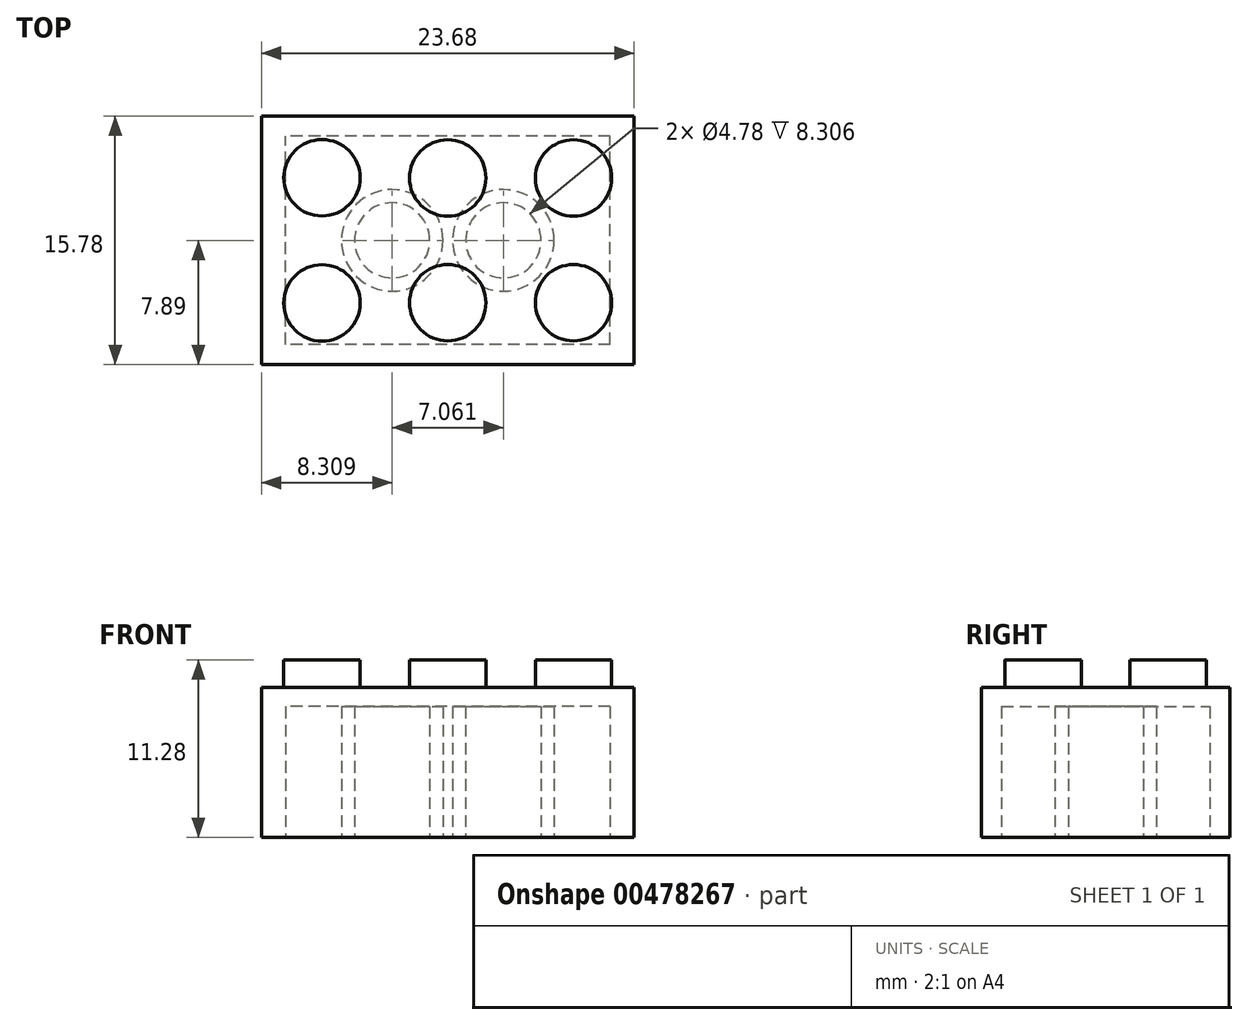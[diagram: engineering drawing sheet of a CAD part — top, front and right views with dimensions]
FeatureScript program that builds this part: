
annotation { "Feature Type Name" : "Feature", "Feature Type Description" : "" }
export const myFeature = defineFeature(function(context is Context, id is Id, definition is map)
    precondition{}
    {
        {
            var Q0;
            Q0=qCreatedBy(makeId("Top.planeOp"),FACE);
            var sketch = newSketch(context, id + "F0", { "sketchPlane" : qUnion([Q0])});
            skLineSegment(sketch, "E0.bottom", {"start": v(11.84, 7.89) * mm, "end": v(-11.84, 7.89) * mm});
            skLineSegment(sketch, "E0.top", {"start": v(11.84, -7.89) * mm, "end": v(-11.84, -7.89) * mm});
            skLineSegment(sketch, "E0.left", {"start": v(11.84, 7.89) * mm, "end": v(11.84, -7.89) * mm});
            skLineSegment(sketch, "E0.right", {"start": v(-11.84, 7.89) * mm, "end": v(-11.84, -7.89) * mm});
            skPoint(sketch, "E0.middle", {"position": v(0, 0) * mm});
            skSolve(sketch);
        }
        {
            var Q0;
            Q0=makeQuery(id+"F0.imprint","IMPRINT",FACE,{"disambiguationData":[TD([[makeQuery(id+"F0.imprint","IMPRINT",EDGE,{"derivedFrom":sQuery(id+"F0.wireOp",EDGE,"E0.bottom")}),1.0]])]});
            extrude(context, id + "F1", {"entities" : qUnion([Q0]), "endBound" : BoundingType.SYMMETRIC, "depth" : 9.52 * mm, "offsetDistance" : 25.4 * mm});
        }
        {
            var Q0;
            Q0=makeQuery(id+"F1.opExtrude","CAP_FACE",FACE,{"disambiguationData":[OSD([sQuery(id+"F0.wireOp",EDGE,"E0.bottom"),sQuery(id+"F0.wireOp",EDGE,"E0.top"),sQuery(id+"F0.wireOp",EDGE,"E0.left"),sQuery(id+"F0.wireOp",EDGE,"E0.right")])],"isStart":false});
            var sketch = newSketch(context, id + "F2", { "sketchPlane" : qUnion([Q0])});
            skCircle(sketch, "E1", {"center": v(-7.99, 3.98) * mm, "radius": 2.43 * mm});
            skCircle(sketch, "E2", {"center": v(0, 3.96) * mm, "radius": 2.43 * mm});
            skCircle(sketch, "E3", {"center": v(7.99, 3.96) * mm, "radius": 2.43 * mm});
            skCircle(sketch, "E4", {"center": v(7.99, -3.96) * mm, "radius": 2.43 * mm});
            skCircle(sketch, "E5", {"center": v(0, -3.96) * mm, "radius": 2.43 * mm});
            skCircle(sketch, "E6", {"center": v(-7.99, -3.98) * mm, "radius": 2.43 * mm});
            skSolve(sketch);
        }
        {
            var Q0;
            Q0 = qSketchRegion(id + "F2", true);
            extrude(context, id + "F3", {"entities" : qUnion([Q0]), "operationType" : NewBodyOperationType.ADD, "depth" : 1.75 * mm, "offsetDistance" : 25.4 * mm});
        }
        {
            var Q0;
            Q0=makeQuery(id+"F1.opExtrude","CAP_FACE",FACE,{"disambiguationData":[OSD([sQuery(id+"F0.wireOp",EDGE,"E0.bottom"),sQuery(id+"F0.wireOp",EDGE,"E0.top"),sQuery(id+"F0.wireOp",EDGE,"E0.left"),sQuery(id+"F0.wireOp",EDGE,"E0.right")])],"isStart":true});
            var sketch = newSketch(context, id + "F4", { "sketchPlane" : qUnion([Q0])});
            skLineSegment(sketch, "E7.bottom", {"start": v(10.31, 6.62) * mm, "end": v(-10.31, 6.62) * mm});
            skLineSegment(sketch, "E7.top", {"start": v(10.31, -6.62) * mm, "end": v(-10.31, -6.62) * mm});
            skLineSegment(sketch, "E7.left", {"start": v(10.31, 6.62) * mm, "end": v(10.31, -6.62) * mm});
            skLineSegment(sketch, "E7.right", {"start": v(-10.31, 6.62) * mm, "end": v(-10.31, -6.62) * mm});
            skPoint(sketch, "E7.middle", {"position": v(0, 0) * mm});
            skSolve(sketch);
        }
        {
            var Q0;
            Q0=makeQuery(id+"F4.imprint","IMPRINT",FACE,{"disambiguationData":[TD([[makeQuery(id+"F4.imprint","IMPRINT",EDGE,{"derivedFrom":sQuery(id+"F4.wireOp",EDGE,"E7.bottom")}),1.0]])]});
            var sketch = newSketch(context, id + "F5", { "sketchPlane" : qUnion([Q0])});
            skCircle(sketch, "E8", {"center": v(-3.53, 0) * mm, "radius": 3.23 * mm});
            skCircle(sketch, "E9", {"center": v(3.53, 0) * mm, "radius": 3.23 * mm});
            skSolve(sketch);
        }
        {
            var Q0;
            Q0=makeQuery(id+"F4.imprint","IMPRINT",FACE,{"disambiguationData":[TD([[makeQuery(id+"F4.imprint","IMPRINT",EDGE,{"derivedFrom":sQuery(id+"F4.wireOp",EDGE,"E7.bottom")}),1.0]])]});
            var sketch = newSketch(context, id + "F6", { "sketchPlane" : qUnion([Q0])});
            skCircle(sketch, "E10", {"center": v(-3.53, 0) * mm, "radius": 2.39 * mm});
            skCircle(sketch, "E11", {"center": v(3.53, 0) * mm, "radius": 2.39 * mm});
            skSolve(sketch);
        }
        {
            var Q0;
            Q0=makeQuery(id+"F4.imprint","IMPRINT",FACE,{"disambiguationData":[TD([[makeQuery(id+"F4.imprint","IMPRINT",EDGE,{"derivedFrom":sQuery(id+"F4.wireOp",EDGE,"E7.bottom")}),1.0]])]});
            extrude(context, id + "F7", {"entities" : qUnion([Q0]), "operationType" : NewBodyOperationType.REMOVE, "oppositeDirection" : true, "depth" : 8.3 * mm, "offsetDistance" : 25.4 * mm});
        }
        {
            var Q0;
            Q0=makeQuery(id+"F5.imprint","IMPRINT",FACE,{"disambiguationData":[TD([[makeQuery(id+"F5.imprint","IMPRINT",EDGE,{"derivedFrom":sQuery(id+"F5.wireOp",EDGE,"E8")}),1.0]])]});
            var Q1;
            Q1=makeQuery(id+"F5.imprint","IMPRINT",FACE,{"disambiguationData":[TD([[makeQuery(id+"F5.imprint","IMPRINT",EDGE,{"derivedFrom":sQuery(id+"F5.wireOp",EDGE,"E9")}),1.0]])]});
            extrude(context, id + "F8", {"entities" : qUnion([Q0, Q1]), "operationType" : NewBodyOperationType.ADD, "depth" : -8.3 * mm, "offsetDistance" : 25.4 * mm});
        }
        {
            var Q0;
            Q0=makeQuery(id+"F6.imprint","IMPRINT",FACE,{"disambiguationData":[TD([[makeQuery(id+"F6.imprint","IMPRINT",EDGE,{"derivedFrom":sQuery(id+"F6.wireOp",EDGE,"E10")}),1.0]])]});
            var Q1;
            Q1=makeQuery(id+"F6.imprint","IMPRINT",FACE,{"disambiguationData":[TD([[makeQuery(id+"F6.imprint","IMPRINT",EDGE,{"derivedFrom":sQuery(id+"F6.wireOp",EDGE,"E11")}),1.0]])]});
            extrude(context, id + "F9", {"entities" : qUnion([Q0, Q1]), "operationType" : NewBodyOperationType.REMOVE, "oppositeDirection" : true, "depth" : 8.3 * mm, "offsetDistance" : 25.4 * mm});
        }
    });
